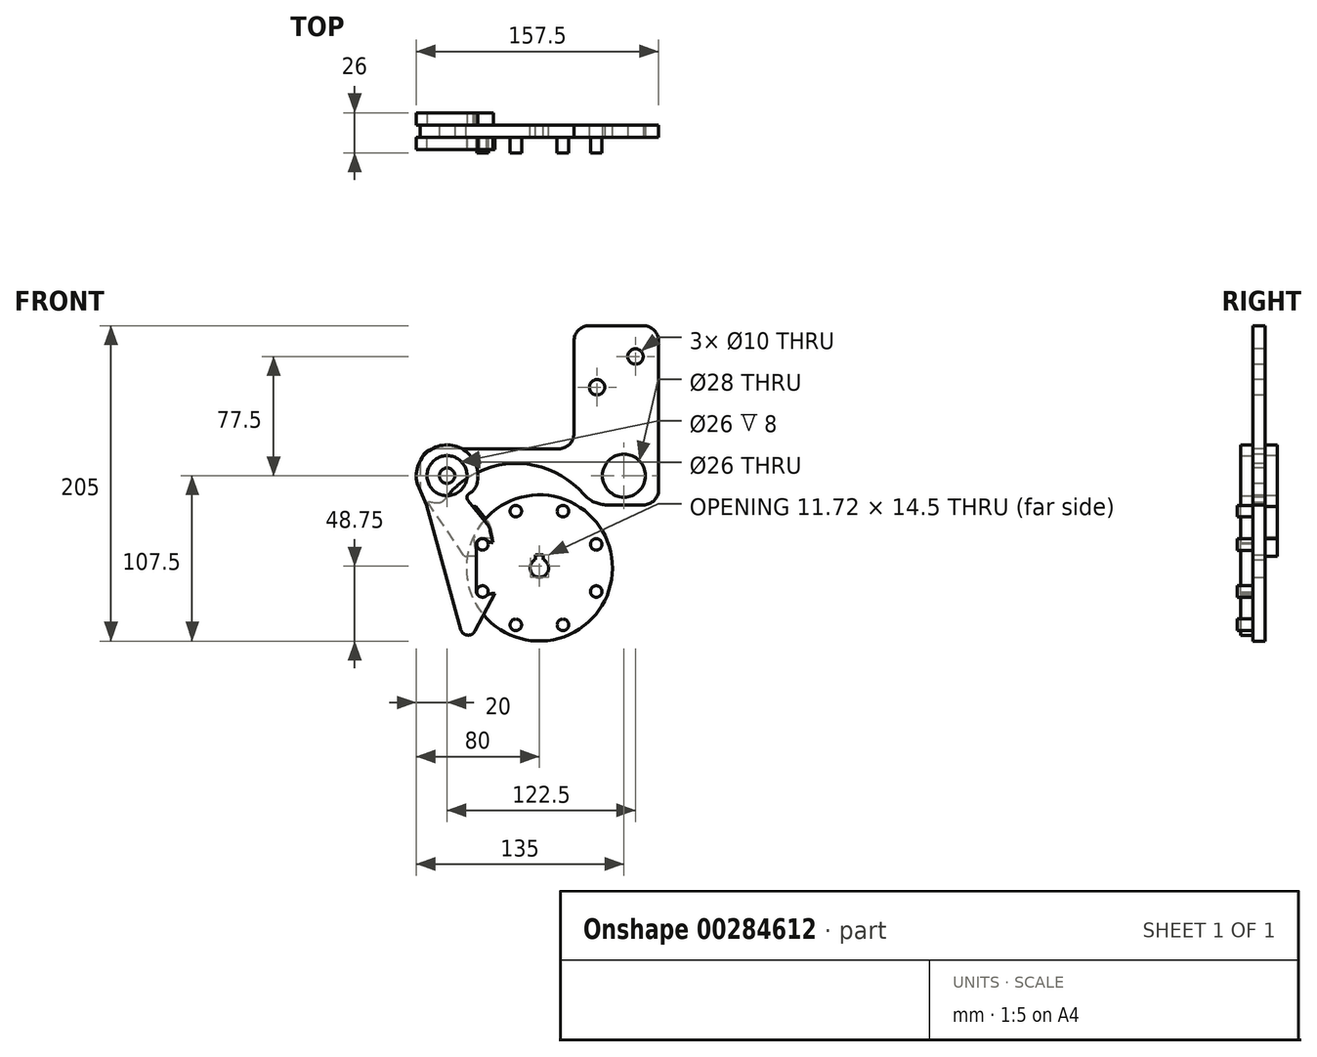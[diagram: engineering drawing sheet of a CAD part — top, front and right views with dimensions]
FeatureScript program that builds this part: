
annotation { "Feature Type Name" : "Feature", "Feature Type Description" : "" }
export const myFeature = defineFeature(function(context is Context, id is Id, definition is map)
    precondition{}
    {
        {
            var Q0;
            Q0=qCreatedBy(makeId("Front.planeOp"),FACE);
            var sketch = newSketch(context, id + "F0", { "sketchPlane" : qUnion([Q0])});
            skCircle(sketch, "E0", {"center": v(0, 0) * mm, "radius": 47.5 * mm});
            skArc(sketch, "E1", {"start": v(-2.5, 5.45) * mm, "mid": v(0, -6) * mm, "end": v(2.5, 5.45) * mm});
            skLineSegment(sketch, "E2.bottom", {"start": v(-2.5, 0) * mm, "end": v(2.5, 0) * mm, "construction": true});
            skLineSegment(sketch, "E2.top", {"start": v(-2.5, 8.5) * mm, "end": v(2.5, 8.5) * mm});
            skLineSegment(sketch, "E2.left", {"start": v(-2.5, 0) * mm, "end": v(-2.5, 3) * mm, "construction": true});
            skLineSegment(sketch, "E2.right", {"start": v(2.5, 0) * mm, "end": v(2.5, 3) * mm, "construction": true});
            skLineSegment(sketch, "E3", {"start": v(-2.5, 3) * mm, "end": v(2.5, 3) * mm, "construction": true});
            skLineSegment(sketch, "E4.trimOffspring", {"start": v(-2.5, 5.45) * mm, "end": v(-2.5, 8.5) * mm});
            skLineSegment(sketch, "E5.trimOffspring", {"start": v(2.5, 5.45) * mm, "end": v(2.5, 8.5) * mm});
            skSolve(sketch);
        }
        {
            var Q0;
            Q0=qSketchRegion(id+"F0",true);
            extrude(context, id + "F1", {"entities" : qUnion([Q0]), "depth" : 5 * mm, "hasSecondDirection" : true, "secondDirectionOppositeDirection" : true, "secondDirectionDepth" : 3 * mm});
        }
        {
            var Q0;
            Q0=makeQuery(id+"F1.opExtrude","CAP_FACE",FACE,{"disambiguationData":[OSD([sQuery(id+"F0.wireOp",EDGE,"E0"),sQuery(id+"F0.wireOp",EDGE,"E1")])],"isStart":false});
            var sketch = newSketch(context, id + "F2", { "sketchPlane" : qUnion([Q0])});
            skCircle(sketch, "E6", {"center": v(0, 0) * mm, "radius": 40 * mm, "construction": true});
            skCircle(sketch, "E7", {"center": v(15.3, 36.96) * mm, "radius": 3.75 * mm});
            skCircle(sketch, "E8.1.0", {"center": v(-15.3, 36.96) * mm, "radius": 3.75 * mm});
            skCircle(sketch, "E8.2.0", {"center": v(-36.96, 15.3) * mm, "radius": 3.75 * mm});
            skCircle(sketch, "E8.3.0", {"center": v(-36.96, -15.3) * mm, "radius": 3.75 * mm});
            skCircle(sketch, "E8.4.0", {"center": v(-15.3, -36.96) * mm, "radius": 3.75 * mm});
            skCircle(sketch, "E8.5.0", {"center": v(15.3, -36.96) * mm, "radius": 3.75 * mm});
            skCircle(sketch, "E8.6.0", {"center": v(36.96, -15.3) * mm, "radius": 3.75 * mm});
            skCircle(sketch, "E8.7.0", {"center": v(36.96, 15.3) * mm, "radius": 3.75 * mm});
            skPoint(sketch, "E9", {"position": v(0, -77) * mm});
            skLineSegment(sketch, "E10", {"start": v(15.3, 36.96) * mm, "end": v(0, 0) * mm, "construction": true});
            skSolve(sketch);
        }
        {
            var Q0;
            Q0=qSketchRegion(id+"F2",true);
            extrude(context, id + "F3", {"entities" : qUnion([Q0]), "operationType" : NewBodyOperationType.ADD, "depth" : 10 * mm});
        }
        {
            var Q0;
            Q0=qCreatedBy(makeId("Right.planeOp"),FACE);
            var sketch = newSketch(context, id + "F4", { "sketchPlane" : qUnion([Q0])});
            skLineSegment(sketch, "E11", {"start": v(-64.67, -77) * mm, "end": v(70.6, -77) * mm});
            skLineSegment(sketch, "E12", {"start": v(-72, 0) * mm, "end": v(117.3, 0) * mm});
            skLineSegment(sketch, "E13", {"start": v(-81.45, 67) * mm, "end": v(84.45, 67) * mm});
            skSolve(sketch);
        }
        {
            var Q0;
            Q0=makeQuery(id+"F1.opExtrude","CAP_FACE",FACE,{"disambiguationData":[OSD([sQuery(id+"F0.wireOp",EDGE,"E0"),sQuery(id+"F0.wireOp",EDGE,"E1")])],"isStart":false});
            var sketch = newSketch(context, id + "F5", { "sketchPlane" : qUnion([Q0])});
            skLineSegment(sketch, "E14", {"start": v(22.5, 147.5) * mm, "end": v(22.5, 87.5) * mm});
            skLineSegment(sketch, "E15", {"start": v(12.5, 77.5) * mm, "end": v(-67.5, 77.5) * mm});
            skLineSegment(sketch, "E16", {"start": v(-77.5, 67.5) * mm, "end": v(-77.5, 52.5) * mm});
            skLineSegment(sketch, "E17", {"start": v(-67.5, 42.5) * mm, "end": v(-65.62, 42.5) * mm});
            skLineSegment(sketch, "E18", {"start": v(67.5, 157.5) * mm, "end": v(32.5, 157.5) * mm});
            skCircle(sketch, "E19", {"center": v(55, 60) * mm, "radius": 14 * mm});
            skCircle(sketch, "E20", {"center": v(-60, 60) * mm, "radius": 5 * mm});
            skCircle(sketch, "E21", {"center": v(62.5, 137.5) * mm, "radius": 5 * mm});
            skCircle(sketch, "E22", {"center": v(37.5, 117.5) * mm, "radius": 5 * mm});
            skPoint(sketch, "E23.visualSharp", {"position": v(-77.5, 77.5) * mm});
            skArc(sketch, "E23.filletArc", {"start": v(-67.5, 77.5) * mm, "mid": v(-74.57, 74.57) * mm, "end": v(-77.5, 67.5) * mm});
            skPoint(sketch, "E24.visualSharp", {"position": v(-77.5, 42.5) * mm});
            skArc(sketch, "E24.filletArc", {"start": v(-77.5, 52.5) * mm, "mid": v(-74.57, 45.43) * mm, "end": v(-67.5, 42.5) * mm});
            skArc(sketch, "E25.filletArc", {"start": v(12.5, 77.5) * mm, "mid": v(19.57, 80.43) * mm, "end": v(22.5, 87.5) * mm});
            skArc(sketch, "E26.filletArc", {"start": v(32.5, 157.5) * mm, "mid": v(25.43, 154.57) * mm, "end": v(22.5, 147.5) * mm});
            skLineSegment(sketch, "E27", {"start": v(77.5, 147.5) * mm, "end": v(77.5, 51) * mm});
            skPoint(sketch, "E28.visualSharp", {"position": v(77.5, 157.5) * mm});
            skArc(sketch, "E28.filletArc", {"start": v(77.5, 147.5) * mm, "mid": v(74.57, 154.57) * mm, "end": v(67.5, 157.5) * mm});
            skPoint(sketch, "E29.visualSharp", {"position": v(77.5, 42.5) * mm});
            skArc(sketch, "E30", {"start": v(28.88, 47.92) * mm, "mid": v(-17.18, 67.96) * mm, "end": v(-61.6, 44.52) * mm});
            skLineSegment(sketch, "E31.trimOffspring", {"start": v(44.02, 41) * mm, "end": v(67.5, 41) * mm});
            skPoint(sketch, "E32.visualSharp", {"position": v(34.02, 41) * mm});
            skArc(sketch, "E32.filletArc", {"start": v(28.88, 47.92) * mm, "mid": v(35.7, 42.81) * mm, "end": v(44.02, 41) * mm});
            skPoint(sketch, "E33.visualSharp", {"position": v(-63.04, 42.5) * mm});
            skArc(sketch, "E33.filletArc", {"start": v(-65.62, 42.5) * mm, "mid": v(-63.37, 43.03) * mm, "end": v(-61.6, 44.52) * mm});
            skPoint(sketch, "E34.visualSharp", {"position": v(77.5, 41) * mm});
            skArc(sketch, "E34.filletArc", {"start": v(67.5, 41) * mm, "mid": v(74.57, 43.93) * mm, "end": v(77.5, 51) * mm});
            skSolve(sketch);
        }
        {
            var Q0;
            Q0=qSketchRegion(id+"F5",true);
            extrude(context, id + "F6", {"entities" : qUnion([Q0]), "oppositeDirection" : true, "depth" : 8 * mm});
        }
        {
            var Q0;
            Q0=makeQuery(id+"F6.opExtrude","CAP_FACE",FACE,{"disambiguationData":[OSD([sQuery(id+"F5.wireOp",EDGE,"6UYUCGHe-v6PJ-xM8n-M9w1-3JftOfFEaaKn"),sQuery(id+"F5.wireOp",EDGE,"E14"),sQuery(id+"F5.wireOp",EDGE,"E15"),sQuery(id+"F5.wireOp",EDGE,"E16"),sQuery(id+"F5.wireOp",EDGE,"E17"),sQuery(id+"F5.wireOp",EDGE,"E18"),sQuery(id+"F5.wireOp",EDGE,"6mSuHOhG-H6Qm-CTf6-0w9e-DGj1v4xZb9vA"),sQuery(id+"F5.wireOp",EDGE,"ny8O01vN-fLXv-90L8-67J4-nZeRYjtkH8Bg"),sQuery(id+"F5.wireOp",EDGE,"AzUAeJxv-LCFY-wvFv-zfbr-WxtbCt1TXvNg"),sQuery(id+"F5.wireOp",EDGE,"E19"),sQuery(id+"F5.wireOp",EDGE,"E20"),sQuery(id+"F5.wireOp",EDGE,"E21"),sQuery(id+"F5.wireOp",EDGE,"E22"),sQuery(id+"F5.wireOp",EDGE,"E23.filletArc"),sQuery(id+"F5.wireOp",EDGE,"E24.filletArc"),sQuery(id+"F5.wireOp",EDGE,"3b4b8c6e-bcbf-47d2-af26-fd6c4953971c.filletArc"),sQuery(id+"F5.wireOp",EDGE,"198be823-ed3f-43f8-8910-094095edfe7a.filletArc"),sQuery(id+"F5.wireOp",EDGE,"060f99cd-04c9-459d-9f5f-5165108c2491.filletArc"),sQuery(id+"F5.wireOp",EDGE,"E25.filletArc"),sQuery(id+"F5.wireOp",EDGE,"E26.filletArc"),sQuery(id+"F5.wireOp",EDGE,"ccb2d568-8b15-4a9f-91dc-9a0a143dbb8f.filletArc")])],"isStart":true});
            var sketch = newSketch(context, id + "F7", { "sketchPlane" : qUnion([Q0])});
            skArc(sketch, "E35", {"start": v(-42.04, 58.82) * mm, "mid": v(-61.83, 77.9) * mm, "end": v(-77.35, 55.22) * mm});
            skCircle(sketch, "E36", {"center": v(-60, 60) * mm, "radius": 13 * mm});
            skLineSegment(sketch, "E37", {"start": v(-28, -15) * mm, "end": v(-46.97, -16) * mm, "construction": true});
            skLineSegment(sketch, "E38", {"start": v(-45.55, 5.65) * mm, "end": v(-42.04, 58.82) * mm});
            skLineSegment(sketch, "E39", {"start": v(-28, -15) * mm, "end": v(-41.85, -41.06) * mm});
            skLineSegment(sketch, "E40", {"start": v(-51.09, -40.04) * mm, "end": v(-77.35, 55.22) * mm});
            skLineSegment(sketch, "E41", {"start": v(-77.35, 55.22) * mm, "end": v(-42.04, 58.82) * mm, "construction": true});
            skPoint(sketch, "E42.visualSharp", {"position": v(-47.75, -52.15) * mm});
            skArc(sketch, "E42.filletArc", {"start": v(-51.09, -40.04) * mm, "mid": v(-46.82, -43.68) * mm, "end": v(-41.85, -41.06) * mm});
            skLineSegment(sketch, "E43", {"start": v(-41, -15.69) * mm, "end": v(-41, -1.69) * mm});
            skPoint(sketch, "E44.visualSharp", {"position": v(-45.98, -1) * mm});
            skArc(sketch, "E45", {"start": v(-41, -15.69) * mm, "mid": v(-38.51, -18.7) * mm, "end": v(-34.64, -18.16) * mm});
            skLineSegment(sketch, "E46", {"start": v(-29.92, -15.1) * mm, "end": v(-28, -15) * mm, "construction": true});
            skPoint(sketch, "E47.visualSharp", {"position": v(-33.07, -15.27) * mm});
            skLineSegment(sketch, "E48", {"start": v(-29.92, -15.1) * mm, "end": v(-28, -15) * mm});
            skLineSegment(sketch, "E49", {"start": v(-45.55, 5.65) * mm, "end": v(-41, -1.69) * mm});
            skLineSegment(sketch, "E50", {"start": v(-28.82, -16.55) * mm, "end": v(-30.49, -16.63) * mm});
            skPoint(sketch, "E51.visualSharp", {"position": v(-33.5, -16.8) * mm});
            skArc(sketch, "E51.filletArc", {"start": v(-30.49, -16.63) * mm, "mid": v(-32.68, -17.08) * mm, "end": v(-34.64, -18.16) * mm});
            skSolve(sketch);
        }
        {
            var Q0;
            Q0=qSketchRegion(id+"F7",true);
            extrude(context, id + "F8", {"entities" : qUnion([Q0]), "depth" : 8 * mm});
        }
        {
            var Q0;
            Q0=qCreatedBy(makeId("Right.planeOp"),FACE);
            cPlane(context, id + "F9", {"entities" : qUnion([Q0]), "cplaneType" : CPlaneType.OFFSET, "offset" : 55 * mm, "width" : 150 * mm, "height" : 150 * mm});
        }
        {
            var Q0;
            Q0=qCreatedBy(id+"F9.planeOp",FACE);
            var sketch = newSketch(context, id + "F10", { "sketchPlane" : qUnion([Q0])});
            skLineSegment(sketch, "E52", {"start": v(-80.65, 60) * mm, "end": v(113, 60) * mm});
            skSolve(sketch);
        }
        {
            var Q0;
            Q0=makeQuery(id+"F1.opExtrude","CAP_FACE",FACE,{"disambiguationData":[OSD([sQuery(id+"F0.wireOp",EDGE,"E0"),sQuery(id+"F0.wireOp",EDGE,"E1")])],"isStart":true});
            var sketch = newSketch(context, id + "F11", { "sketchPlane" : qUnion([Q0])});
            skCircle(sketch, "E53", {"center": v(60, 60) * mm, "radius": 13 * mm});
            skArc(sketch, "E54", {"start": v(76.54, 48.76) * mm, "mid": v(59.86, 80) * mm, "end": v(43.62, 48.53) * mm});
            skLineSegment(sketch, "E55", {"start": v(31.73, 26.5) * mm, "end": v(30, 19) * mm});
            skLineSegment(sketch, "E56", {"start": v(30, 19) * mm, "end": v(43, 20) * mm});
            skLineSegment(sketch, "E57", {"start": v(43, 20) * mm, "end": v(41, 7.5) * mm});
            skLineSegment(sketch, "E58", {"start": v(41, 7.5) * mm, "end": v(47.44, 7.5) * mm});
            skLineSegment(sketch, "E59", {"start": v(49.1, 8.38) * mm, "end": v(76.54, 48.76) * mm});
            skPoint(sketch, "E60.visualSharp", {"position": v(48.5, 7.5) * mm});
            skArc(sketch, "E60.filletArc", {"start": v(47.44, 7.5) * mm, "mid": v(48.38, 7.73) * mm, "end": v(49.1, 8.38) * mm});
            skPoint(sketch, "E61", {"position": v(32.25, 28.74) * mm});
            skLineSegment(sketch, "E62", {"start": v(33.7, 30.54) * mm, "end": v(43.4, 42.52) * mm});
            skPoint(sketch, "E63.visualSharp", {"position": v(46, 45.72) * mm});
            skArc(sketch, "E63.filletArc", {"start": v(43.4, 42.52) * mm, "mid": v(44.52, 45.49) * mm, "end": v(43.62, 48.53) * mm});
            skArc(sketch, "E64.filletArc", {"start": v(33.7, 30.54) * mm, "mid": v(32.49, 28.63) * mm, "end": v(31.73, 26.5) * mm});
            skSolve(sketch);
        }
        {
            var Q0;
            Q0=qSketchRegion(id+"F11",true);
            extrude(context, id + "F12", {"entities" : qUnion([Q0]), "depth" : 8 * mm});
        }
        {
            var Q0;
            Q0=makeQuery(id+"F8.opExtrude","CAP_FACE",FACE,{"disambiguationData":[OSD([sQuery(id+"F7.wireOp",EDGE,"E35"),sQuery(id+"F7.wireOp",EDGE,"E36"),sQuery(id+"F7.wireOp",EDGE,"E37"),sQuery(id+"F7.wireOp",EDGE,"E38"),sQuery(id+"F7.wireOp",EDGE,"E39"),sQuery(id+"F7.wireOp",EDGE,"E40"),sQuery(id+"F7.wireOp",EDGE,"E42.filletArc")])],"isStart":true});
            var sketch = newSketch(context, id + "F13", { "sketchPlane" : qUnion([Q0])});
            skCircle(sketch, "E65", {"center": v(60, 60) * mm, "radius": 13 * mm});
            skArc(sketch, "E66", {"start": v(78.28, 51.89) * mm, "mid": v(57.48, 79.84) * mm, "end": v(44.33, 47.57) * mm});
            skLineSegment(sketch, "E67", {"start": v(32, 24.39) * mm, "end": v(30, 15) * mm});
            skLineSegment(sketch, "E68", {"start": v(30, 15) * mm, "end": v(41, 16) * mm, "construction": true});
            skLineSegment(sketch, "E69", {"start": v(41, -15.69) * mm, "end": v(47, -15.69) * mm});
            skLineSegment(sketch, "E70", {"start": v(48.83, -14.5) * mm, "end": v(78.28, 51.89) * mm});
            skPoint(sketch, "E71.visualSharp", {"position": v(48.3, -15.69) * mm});
            skArc(sketch, "E71.filletArc", {"start": v(47, -15.69) * mm, "mid": v(48.09, -15.36) * mm, "end": v(48.83, -14.5) * mm});
            skPoint(sketch, "E72", {"position": v(32.5, 26.74) * mm});
            skLineSegment(sketch, "E73", {"start": v(34, 28.6) * mm, "end": v(44.3, 41.32) * mm});
            skPoint(sketch, "E74.visualSharp", {"position": v(47.07, 44.74) * mm});
            skArc(sketch, "E74.filletArc", {"start": v(44.3, 41.32) * mm, "mid": v(45.41, 44.44) * mm, "end": v(44.33, 47.57) * mm});
            skArc(sketch, "E75.filletArc", {"start": v(34, 28.6) * mm, "mid": v(32.75, 26.62) * mm, "end": v(32, 24.39) * mm});
            skLineSegment(sketch, "E76", {"start": v(41, 16) * mm, "end": v(41, -15.69) * mm});
            skArc(sketch, "E77", {"start": v(41, 16) * mm, "mid": v(38.4, 18.92) * mm, "end": v(34.55, 18.23) * mm});
            skLineSegment(sketch, "E78", {"start": v(30, 15) * mm, "end": v(29.95, 15) * mm});
            skPoint(sketch, "E79.visualSharp", {"position": v(33.1, 15.28) * mm});
            skArc(sketch, "E79.filletArc", {"start": v(29.95, 15) * mm, "mid": v(32.1, 15.7) * mm, "end": v(33.72, 17.3) * mm, "construction": true});
            skLineSegment(sketch, "E80", {"start": v(30.33, 16.54) * mm, "end": v(30.46, 16.55) * mm});
            skPoint(sketch, "E81.visualSharp", {"position": v(33.46, 16.82) * mm});
            skArc(sketch, "E81.filletArc", {"start": v(30.46, 16.55) * mm, "mid": v(32.63, 17.08) * mm, "end": v(34.55, 18.23) * mm});
            skSolve(sketch);
        }
        {
            var Q0;
            Q0=qSketchRegion(id+"F13",true);
            extrude(context, id + "F14", {"entities" : qUnion([Q0]), "operationType" : NewBodyOperationType.ADD, "oppositeDirection" : true, "depth" : 8 * mm});
        }
        {
            var Q0;
            Q0=makeQuery(id+"F14.boolean.opBoolean","MERGE",FACE,{"derivedFrom":[makeQuery(id+"F8.opExtrude","CAP_FACE",FACE,{"disambiguationData":[OSD([sQuery(id+"F7.wireOp",EDGE,"E35"),sQuery(id+"F7.wireOp",EDGE,"E36"),sQuery(id+"F7.wireOp",EDGE,"E37"),sQuery(id+"F7.wireOp",EDGE,"E38"),sQuery(id+"F7.wireOp",EDGE,"E39"),sQuery(id+"F7.wireOp",EDGE,"E40"),sQuery(id+"F7.wireOp",EDGE,"E42.filletArc")])],"isStart":false}),makeQuery(id+"F14.opExtrude","CAP_FACE",FACE,{"disambiguationData":[OSD([sQuery(id+"F13.wireOp",EDGE,"E65"),sQuery(id+"F13.wireOp",EDGE,"E66"),sQuery(id+"F13.wireOp",EDGE,"E67"),sQuery(id+"F13.wireOp",EDGE,"E68"),sQuery(id+"F13.wireOp",EDGE,"e21be7fb-0efc-4c43-9bb7-7c38f81e5f88"),sQuery(id+"F13.wireOp",EDGE,"E69"),sQuery(id+"F13.wireOp",EDGE,"E70"),sQuery(id+"F13.wireOp",EDGE,"E71.filletArc"),sQuery(id+"F13.wireOp",EDGE,"E73"),sQuery(id+"F13.wireOp",EDGE,"E74.filletArc"),sQuery(id+"F13.wireOp",EDGE,"E75.filletArc")])],"isStart":false})]});
            var sketch = newSketch(context, id + "F15", { "sketchPlane" : qUnion([Q0])});
            skLineSegment(sketch, "E82", {"start": v(-43.28, 40.06) * mm, "end": v(-46.42, 43.94) * mm});
            skPoint(sketch, "E83.visualSharp", {"position": v(-51.73, 50.5) * mm});
            skArc(sketch, "E83.filletArc", {"start": v(-45.55, 48.45) * mm, "mid": v(-47.04, 46.4) * mm, "end": v(-46.42, 43.94) * mm});
            skArc(sketch, "E84", {"start": v(-40.8, 54.4) * mm, "mid": v(-76.82, 70.82) * mm, "end": v(-46.93, 44.86) * mm, "construction": true});
            skPoint(sketch, "E85.visualSharp", {"position": v(-43.46, 48.76) * mm});
            skArc(sketch, "E85.filletArc", {"start": v(-45.55, 48.45) * mm, "mid": v(-42.59, 50.95) * mm, "end": v(-40.8, 54.4) * mm});
            skLineSegment(sketch, "E86", {"start": v(-40.8, 54.4) * mm, "end": v(-35.28, 54.4) * mm});
            skLineSegment(sketch, "E87", {"start": v(-35.28, 54.4) * mm, "end": v(-35.28, 40.06) * mm});
            skLineSegment(sketch, "E88", {"start": v(-43.28, 40.06) * mm, "end": v(-35.28, 40.06) * mm});
            skSolve(sketch);
        }
        {
            var Q0;
            Q0=qSketchRegion(id+"F15",true);
            extrude(context, id + "F16", {"entities" : qUnion([Q0]), "operationType" : NewBodyOperationType.REMOVE, "oppositeDirection" : true, "depth" : 25 * mm});
        }
    });
